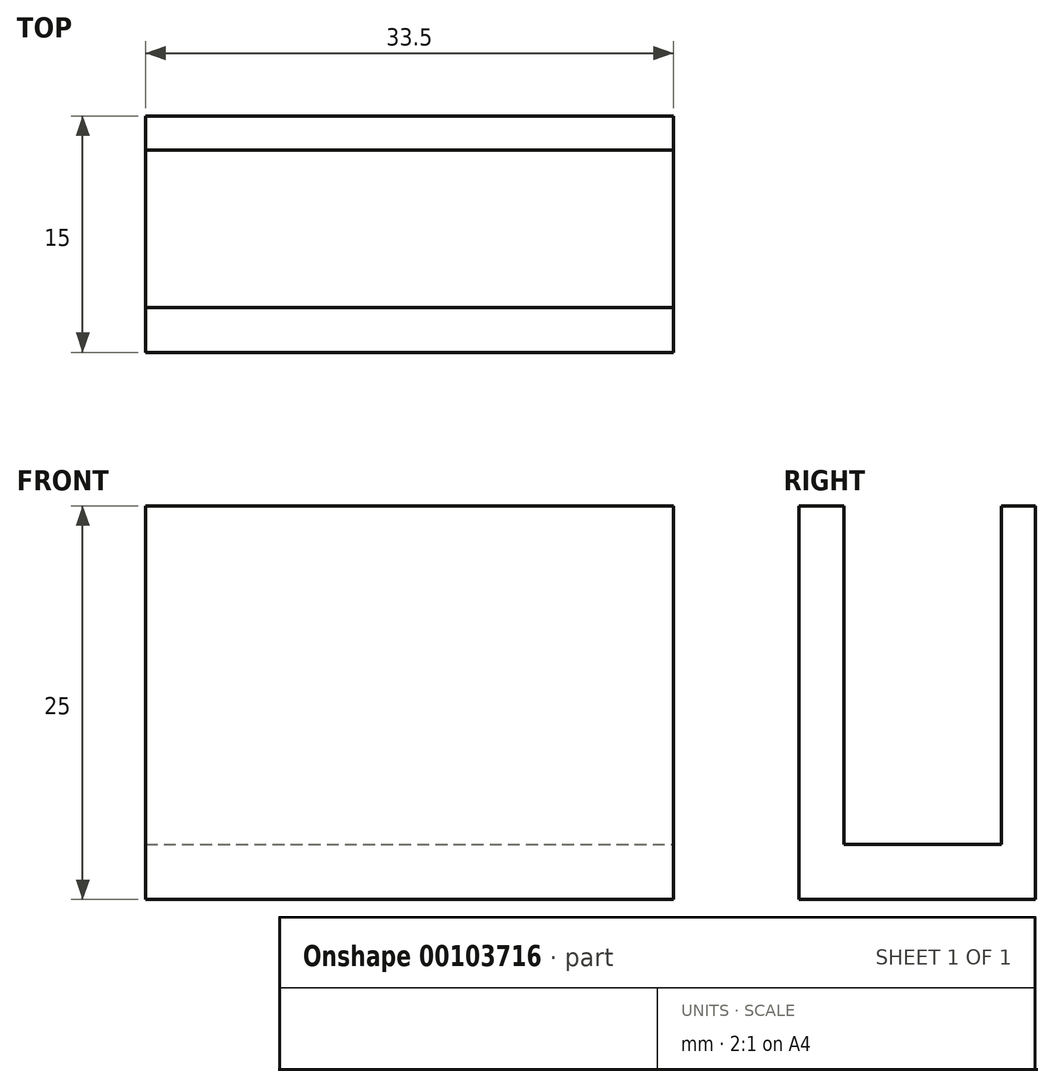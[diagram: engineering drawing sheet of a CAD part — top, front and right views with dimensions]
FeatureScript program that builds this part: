
annotation { "Feature Type Name" : "Feature", "Feature Type Description" : "" }
export const myFeature = defineFeature(function(context is Context, id is Id, definition is map)
    precondition{}
    {
        {
            var Q0;
            Q0=qCreatedBy(makeId("Front.planeOp"),FACE);
            var sketch = newSketch(context, id + "F0", { "sketchPlane" : qUnion([Q0])});
            skLineSegment(sketch, "E0.bottom", {"start": v(-16.75, 12.5) * mm, "end": v(16.75, 12.5) * mm});
            skLineSegment(sketch, "E0.top", {"start": v(-16.75, -12.5) * mm, "end": v(16.75, -12.5) * mm});
            skLineSegment(sketch, "E0.left", {"start": v(-16.75, 12.5) * mm, "end": v(-16.75, -12.5) * mm});
            skLineSegment(sketch, "E0.right", {"start": v(16.75, 12.5) * mm, "end": v(16.75, -12.5) * mm});
            skPoint(sketch, "E0.middle", {"position": v(0, 0) * mm});
            skSolve(sketch);
        }
        {
            var Q0;
            Q0=makeQuery(id+"F0.imprint","IMPRINT",FACE,{"disambiguationData":[TD([[makeQuery(id+"F0.imprint","IMPRINT",EDGE,{"derivedFrom":sQuery(id+"F0.wireOp",EDGE,"E0.bottom")}),-1.0]])]});
            extrude(context, id + "F1", {"entities" : qUnion([Q0]), "depth" : 15 * mm});
        }
        {
            var Q0;
            Q0=makeQuery(id+"F1.opExtrude","SWEPT_FACE",FACE,{"disambiguationData":[OSD([sQuery(id+"F0.wireOp",EDGE,"E0.bottom")])]});
            var sketch = newSketch(context, id + "F2", { "sketchPlane" : qUnion([Q0])});
            skLineSegment(sketch, "E1.bottom", {"start": v(-16.75, -12.17) * mm, "end": v(16.75, -12.17) * mm});
            skLineSegment(sketch, "E1.top", {"start": v(-16.75, -2.17) * mm, "end": v(16.75, -2.17) * mm});
            skLineSegment(sketch, "E1.left", {"start": v(-16.75, -12.17) * mm, "end": v(-16.75, -2.17) * mm});
            skLineSegment(sketch, "E1.right", {"start": v(16.75, -12.17) * mm, "end": v(16.75, -2.17) * mm});
            skSolve(sketch);
        }
        {
            var Q0;
            Q0=makeQuery(id+"F2.imprint","IMPRINT",FACE,{"disambiguationData":[TD([[makeQuery(id+"F2.imprint","IMPRINT",EDGE,{"derivedFrom":sQuery(id+"F2.wireOp",EDGE,"E1.bottom")}),1.0]])]});
            extrude(context, id + "F3", {"entities" : qUnion([Q0]), "operationType" : NewBodyOperationType.REMOVE, "oppositeDirection" : true, "depth" : 21.5 * mm});
        }
    });
